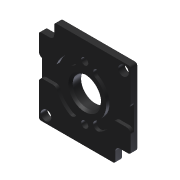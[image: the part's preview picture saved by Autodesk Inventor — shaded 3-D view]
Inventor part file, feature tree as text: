
AUTODESK INVENTOR PART (.ipt)
format: ipt  version: 2013 (Build 170138000, 138)  size: 246,272 bytes
history: native  units: in
note: dims shown in document units (in); Inventor stores cm internally (conversion verified against a paired STEP export)
features: fillet x1, other x1, imported_body x1
ambient origin geometry x8: Origin, YZ Plane, XZ Plane, XY Plane, X Axis, Y Axis, Z Axis, Center Point
feature tree (3):
  fillet  "Fillet4"  [1 undecoded]
  other  "217-2822-550 Mounting Plate STEP1"
  imported_body  "Base1"
note: 1 required parameter value undecoded (feature->parameter linkage not recoverable at this tier; creation-order binding heuristic only, values carry confidence <= 0.55)
